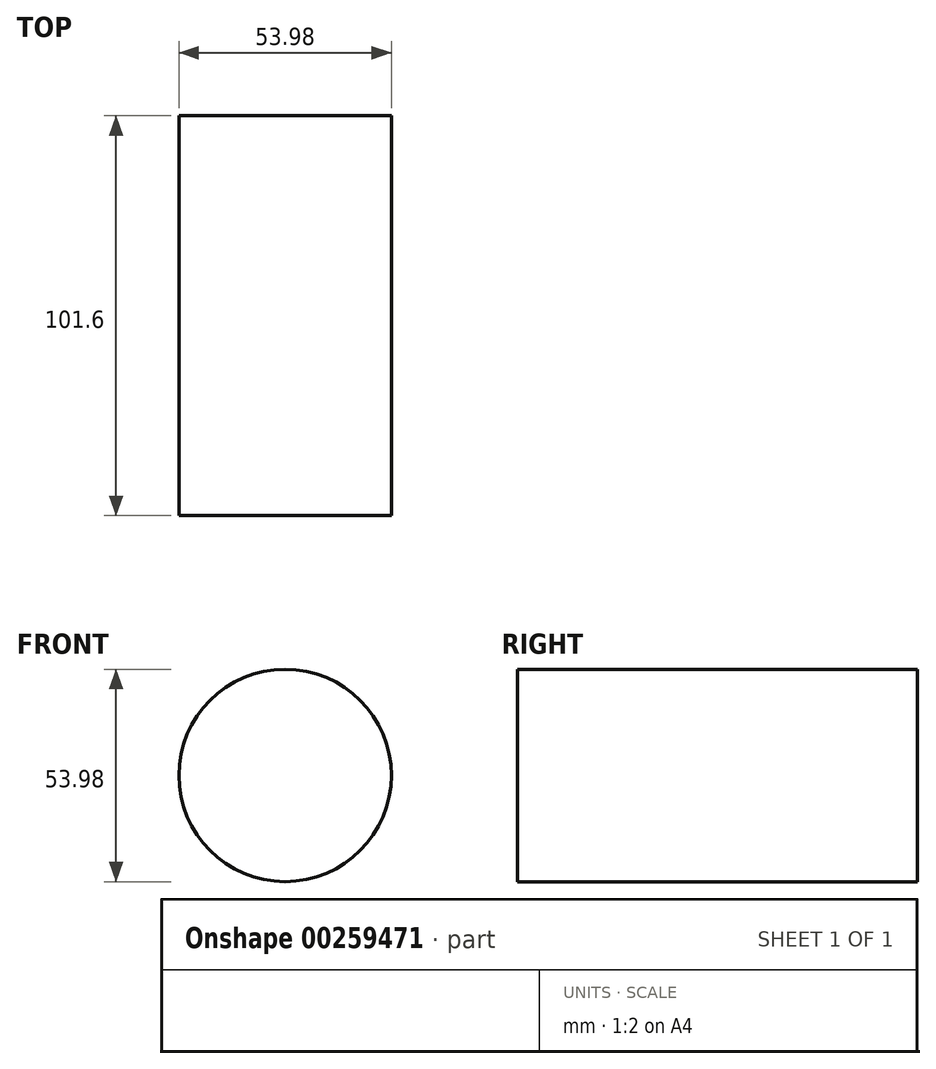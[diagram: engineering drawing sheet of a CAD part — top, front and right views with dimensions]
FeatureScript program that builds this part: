
annotation { "Feature Type Name" : "Feature", "Feature Type Description" : "" }
export const myFeature = defineFeature(function(context is Context, id is Id, definition is map)
    precondition{}
    {
        {
            var Q0;
            Q0=qCreatedBy(makeId("Front.planeOp"),FACE);
            var sketch = newSketch(context, id + "F0", { "sketchPlane" : qUnion([Q0])});
            skCircle(sketch, "E0", {"center": v(0, 0) * mm, "radius": 26.99 * mm});
            skSolve(sketch);
        }
        {
            var Q0;
            Q0=makeQuery(id+"F0.imprint","IMPRINT",FACE,{"disambiguationData":[TD([[makeQuery(id+"F0.imprint","IMPRINT",EDGE,{"derivedFrom":sQuery(id+"F0.wireOp",EDGE,"E0")}),1.0]])]});
            extrude(context, id + "F1", {"entities" : qUnion([Q0]), "depth" : 101.6 * mm});
        }
    });
